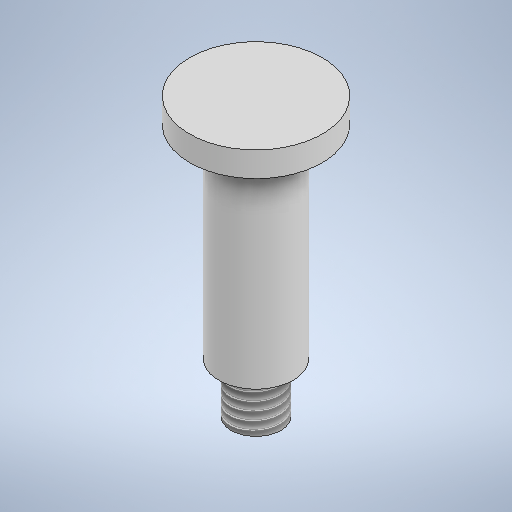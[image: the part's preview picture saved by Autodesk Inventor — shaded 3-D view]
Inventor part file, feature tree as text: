
AUTODESK INVENTOR PART (.ipt)
format: ipt  version: 2025.1 (Build 291241000, 241)  size: 259,584 bytes
history: native  units: mm
features: revolve x1, thread x1, sketch x1
ambient origin geometry x8: Origin, YZ Plane, XZ Plane, XY Plane, X Axis, Y Axis, Z Axis, Center Point
bodies: Solid1 (feature_tree)
feature tree (3):
  revolve  "Revolution1"  [1 undecoded]
  thread  "Thread1"  [1 undecoded]
  sketch  "Sketch1"  dims[d0=6.0mm d1=6.0mm d2=24.5mm d3=3.0mm d4=9.0mm d5=16.0mm d6=90.0deg d7=12.0mm d8=0.0mm]
note: 2 required parameter values undecoded (feature->parameter linkage not recoverable at this tier; creation-order binding heuristic only, values carry confidence <= 0.55)